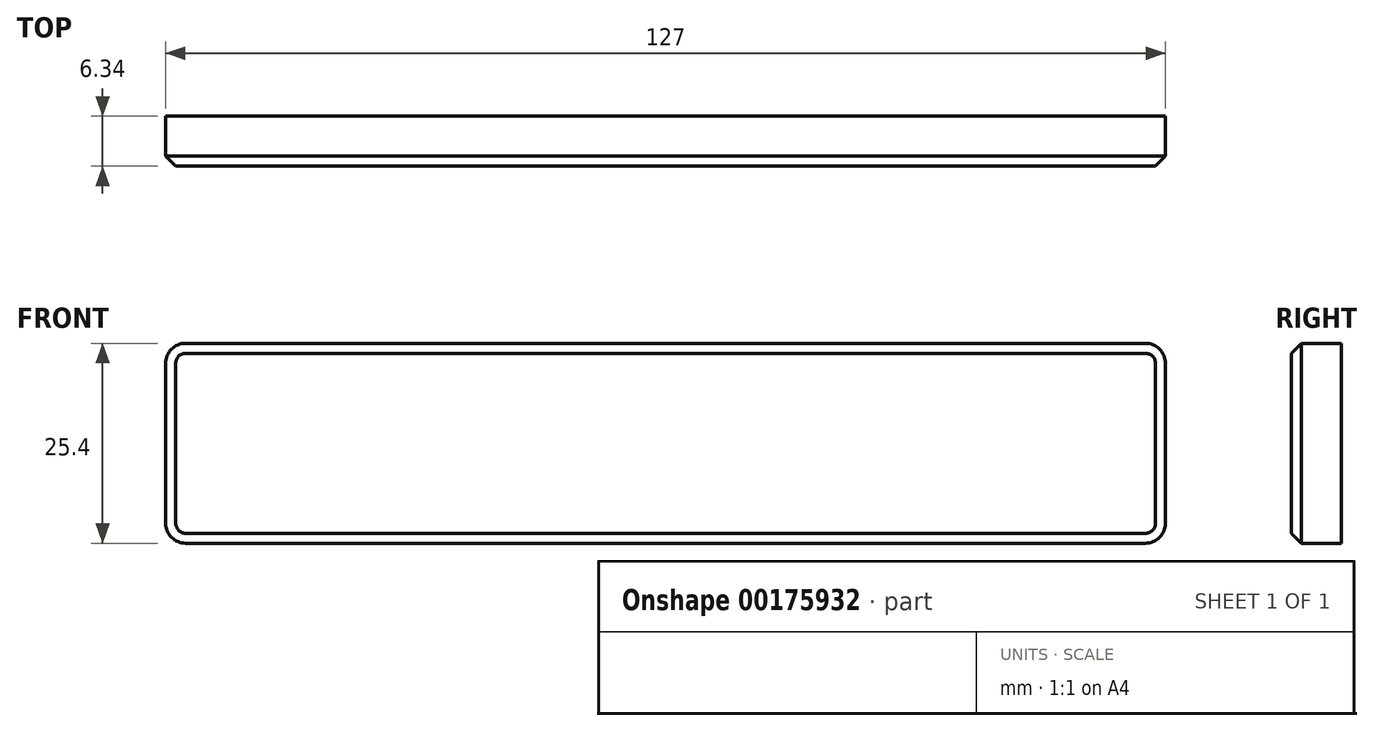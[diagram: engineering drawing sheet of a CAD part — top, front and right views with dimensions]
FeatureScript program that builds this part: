
annotation { "Feature Type Name" : "Feature", "Feature Type Description" : "" }
export const myFeature = defineFeature(function(context is Context, id is Id, definition is map)
    precondition{}
    {
        {
            var Q0;
            Q0=qCreatedBy(makeId("Front.planeOp"),FACE);
            var sketch = newSketch(context, id + "F0", { "sketchPlane" : qUnion([Q0])});
            skLineSegment(sketch, "E0.bottom", {"start": v(-63.5, 12.7) * mm, "end": v(63.5, 12.7) * mm});
            skLineSegment(sketch, "E0.top", {"start": v(-63.5, -12.7) * mm, "end": v(63.5, -12.7) * mm});
            skLineSegment(sketch, "E0.left", {"start": v(-63.5, 12.7) * mm, "end": v(-63.5, -12.7) * mm});
            skLineSegment(sketch, "E0.right", {"start": v(63.5, 12.7) * mm, "end": v(63.5, -12.7) * mm});
            skPoint(sketch, "E0.middle", {"position": v(0, 0) * mm});
            skSolve(sketch);
        }
        {
            var Q0;
            Q0=makeQuery(id+"F0.imprint","IMPRINT",FACE,{"disambiguationData":[TD([[makeQuery(id+"F0.imprint","IMPRINT",EDGE,{"derivedFrom":sQuery(id+"F0.wireOp",EDGE,"E0.bottom")}),-1.0]])]});
            extrude(context, id + "F1", {"entities" : qUnion([Q0]), "endBound" : BoundingType.SYMMETRIC, "depth" : 6.35 * mm});
        }
        {
            var Q0;
            Q0=makeQuery(id+"F1.opExtrude","SWEPT_EDGE",EDGE,{"disambiguationData":[OSD([sQuery(id+"F0.wireOp",EDGE,"E0.top"),sQuery(id+"F0.wireOp",EDGE,"E0.left")])]});
            var Q1;
            Q1=makeQuery(id+"F1.opExtrude","SWEPT_EDGE",EDGE,{"disambiguationData":[OSD([sQuery(id+"F0.wireOp",EDGE,"E0.top"),sQuery(id+"F0.wireOp",EDGE,"E0.right")])]});
            var Q2;
            Q2=makeQuery(id+"F1.opExtrude","SWEPT_EDGE",EDGE,{"disambiguationData":[OSD([sQuery(id+"F0.wireOp",EDGE,"E0.bottom"),sQuery(id+"F0.wireOp",EDGE,"E0.left")])]});
            var Q3;
            Q3=makeQuery(id+"F1.opExtrude","SWEPT_EDGE",EDGE,{"disambiguationData":[OSD([sQuery(id+"F0.wireOp",EDGE,"E0.bottom"),sQuery(id+"F0.wireOp",EDGE,"E0.right")])]});
            fillet(context, id + "F2", {"entities" : qUnion([Q0, Q1, Q2, Q3]), "radius" : 2.54 * mm, "tangentPropagation" : true, "allowEdgeOverflow" : false});
        }
        {
            var Q0;
            Q0=makeQuery(id+"F1.opExtrude","CAP_EDGE",EDGE,{"disambiguationData":[OSD([sQuery(id+"F0.wireOp",EDGE,"E0.bottom")])],"isStart":false});
            var Q1;
            Q1=makeQuery(id+"F1.opExtrude","CAP_EDGE",EDGE,{"disambiguationData":[OSD([sQuery(id+"F0.wireOp",EDGE,"E0.left")])],"isStart":false});
            var Q2;
            Q2=makeQuery(id+"F1.opExtrude","CAP_EDGE",EDGE,{"disambiguationData":[OSD([sQuery(id+"F0.wireOp",EDGE,"E0.top")])],"isStart":false});
            var Q3;
            Q3=makeQuery(id+"F1.opExtrude","CAP_EDGE",EDGE,{"disambiguationData":[OSD([sQuery(id+"F0.wireOp",EDGE,"E0.right")])],"isStart":false});
            var Q4;
            {var subQ0=sQuery(id+"F0.wireOp",EDGE,"E0.right");var subQ1=sQuery(id+"F0.wireOp",EDGE,"E0.bottom");Q4=makeQuery(id+"F2.opFillet","BLEND_EDGE",EDGE,{"blendedFrom":[makeQuery(id+"F1.opExtrude","SWEPT_EDGE",EDGE,{"disambiguationData":[OSD([subQ1,subQ0])]}),makeQuery(id+"F1.opExtrude","CAP_FACE",FACE,{"disambiguationData":[OSD([subQ1,sQuery(id+"F0.wireOp",EDGE,"E0.top"),sQuery(id+"F0.wireOp",EDGE,"E0.left"),subQ0])],"isStart":false})],"blendedInto":[makeQuery(id+"F1.opExtrude","CAP_FACE",FACE,{"disambiguationData":[OSD([subQ1,sQuery(id+"F0.wireOp",EDGE,"E0.top"),sQuery(id+"F0.wireOp",EDGE,"E0.left"),subQ0])],"isStart":false})]});}
            var Q5;
            {var subQ0=sQuery(id+"F0.wireOp",EDGE,"E0.left");var subQ1=sQuery(id+"F0.wireOp",EDGE,"E0.bottom");Q5=makeQuery(id+"F2.opFillet","BLEND_EDGE",EDGE,{"blendedFrom":[makeQuery(id+"F1.opExtrude","SWEPT_EDGE",EDGE,{"disambiguationData":[OSD([subQ1,subQ0])]}),makeQuery(id+"F1.opExtrude","CAP_FACE",FACE,{"disambiguationData":[OSD([subQ1,sQuery(id+"F0.wireOp",EDGE,"E0.top"),subQ0,sQuery(id+"F0.wireOp",EDGE,"E0.right")])],"isStart":false})],"blendedInto":[makeQuery(id+"F1.opExtrude","CAP_FACE",FACE,{"disambiguationData":[OSD([subQ1,sQuery(id+"F0.wireOp",EDGE,"E0.top"),subQ0,sQuery(id+"F0.wireOp",EDGE,"E0.right")])],"isStart":false})]});}
            var Q6;
            {var subQ0=sQuery(id+"F0.wireOp",EDGE,"E0.left");var subQ1=sQuery(id+"F0.wireOp",EDGE,"E0.top");Q6=makeQuery(id+"F2.opFillet","BLEND_EDGE",EDGE,{"blendedFrom":[makeQuery(id+"F1.opExtrude","SWEPT_EDGE",EDGE,{"disambiguationData":[OSD([subQ1,subQ0])]}),makeQuery(id+"F1.opExtrude","CAP_FACE",FACE,{"disambiguationData":[OSD([sQuery(id+"F0.wireOp",EDGE,"E0.bottom"),subQ1,subQ0,sQuery(id+"F0.wireOp",EDGE,"E0.right")])],"isStart":false})],"blendedInto":[makeQuery(id+"F1.opExtrude","CAP_FACE",FACE,{"disambiguationData":[OSD([sQuery(id+"F0.wireOp",EDGE,"E0.bottom"),subQ1,subQ0,sQuery(id+"F0.wireOp",EDGE,"E0.right")])],"isStart":false})]});}
            var Q7;
            {var subQ0=sQuery(id+"F0.wireOp",EDGE,"E0.right");var subQ1=sQuery(id+"F0.wireOp",EDGE,"E0.top");Q7=makeQuery(id+"F2.opFillet","BLEND_EDGE",EDGE,{"blendedFrom":[makeQuery(id+"F1.opExtrude","SWEPT_EDGE",EDGE,{"disambiguationData":[OSD([subQ1,subQ0])]}),makeQuery(id+"F1.opExtrude","CAP_FACE",FACE,{"disambiguationData":[OSD([sQuery(id+"F0.wireOp",EDGE,"E0.bottom"),subQ1,sQuery(id+"F0.wireOp",EDGE,"E0.left"),subQ0])],"isStart":false})],"blendedInto":[makeQuery(id+"F1.opExtrude","CAP_FACE",FACE,{"disambiguationData":[OSD([sQuery(id+"F0.wireOp",EDGE,"E0.bottom"),subQ1,sQuery(id+"F0.wireOp",EDGE,"E0.left"),subQ0])],"isStart":false})]});}
            chamfer(context, id + "F3", {"entities" : qUnion([Q0, Q1, Q2, Q3, Q4, Q5, Q6, Q7]), "width" : 1.27 * mm, "tangentPropagation" : true});
        }
    });
